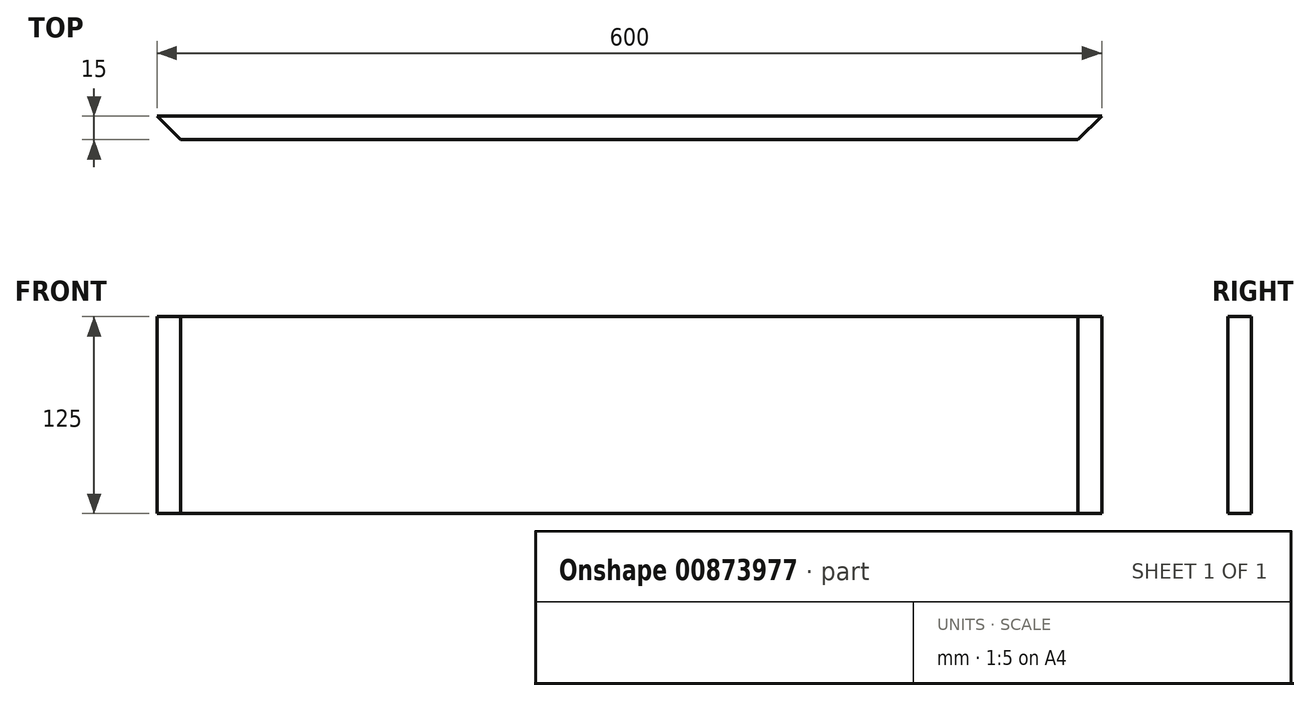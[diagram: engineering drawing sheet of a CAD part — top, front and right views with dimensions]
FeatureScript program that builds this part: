
annotation { "Feature Type Name" : "Feature", "Feature Type Description" : "" }
export const myFeature = defineFeature(function(context is Context, id is Id, definition is map)
    precondition{}
    {
        {
            var Q0;
            Q0=qCreatedBy(makeId("Front.planeOp"),FACE);
            var sketch = newSketch(context, id + "F0", { "sketchPlane" : qUnion([Q0])});
            skLineSegment(sketch, "E0.bottom", {"start": v(0, 0) * mm, "end": v(600, 0) * mm});
            skLineSegment(sketch, "E0.top", {"start": v(0, 125) * mm, "end": v(600, 125) * mm});
            skLineSegment(sketch, "E0.left", {"start": v(0, 0) * mm, "end": v(0, 125) * mm});
            skLineSegment(sketch, "E0.right", {"start": v(600, 0) * mm, "end": v(600, 125) * mm});
            skSolve(sketch);
        }
        {
            var Q0;
            Q0=makeQuery(id+"F0.imprint","IMPRINT",FACE,{"disambiguationData":[TD([[makeQuery(id+"F0.imprint","IMPRINT",EDGE,{"derivedFrom":sQuery(id+"F0.wireOp",EDGE,"E0.bottom")}),1.0]])]});
            extrude(context, id + "F1", {"entities" : qUnion([Q0]), "depth" : 15 * mm, "offsetDistance" : 25 * mm});
        }
        {
            var Q0;
            Q0=makeQuery(id+"F1.opExtrude","SWEPT_FACE",FACE,{"disambiguationData":[OSD([sQuery(id+"F0.wireOp",EDGE,"E0.top")])]});
            var sketch = newSketch(context, id + "F2", { "sketchPlane" : qUnion([Q0])});
            skLineSegment(sketch, "E1", {"start": v(0, 0) * mm, "end": v(15, -15) * mm});
            skLineSegment(sketch, "E2", {"start": v(300, 0) * mm, "end": v(300, -15) * mm, "construction": true});
            skLineSegment(sketch, "E3.MirrorCS", {"start": v(600, 0) * mm, "end": v(585, -15) * mm});
            skSolve(sketch);
        }
        {
            var Q0;
            Q0 = qSketchRegion(id + "F2", true);
            var Q1;
            {var subQ0=sQuery(id+"F2.wireOp",EDGE,"E1");Q1=makeQuery(id+"F2.imprint","IMPRINT",FACE,{"disambiguationData":[TD([[makeQuery(id+"F2.imprint","IMPRINT",EDGE,{"derivedFrom":subQ0}),-1.0]])]});}
            var Q2;
            {var subQ0=sQuery(id+"F2.wireOp",EDGE,"E3.MirrorCS");Q2=makeQuery(id+"F2.imprint","IMPRINT",FACE,{"disambiguationData":[TD([[makeQuery(id+"F2.imprint","IMPRINT",EDGE,{"derivedFrom":subQ0}),1.0]])]});}
            extrude(context, id + "F3", {"entities" : qUnion([Q0, Q1, Q2]), "operationType" : NewBodyOperationType.REMOVE, "endBound" : BoundingType.THROUGH_ALL, "oppositeDirection" : true, "depth" : 25 * mm, "offsetDistance" : 25 * mm});
        }
    });
